# Revit family: Sanitary_Toilet-Cisterns_Sanindusa_Easy-3-6L-Flushing-Plate
name_source: partatom
category: Plumbing Fixtures
revit_build: Autodesk Revit 2018 (Build: 20170223_1515(x64)
units: mm (PartAtom-declared; Revit-internal decimal feet)

## family parameters
Always vertical = Yes
Cut with Voids When Loaded = No
OmniClass Number = 23.45.00.00
OmniClass Title = Sanitary, Laundry, and Cleaning Equipment
Part Type = Normal
Room Calculation Point = No
Round Connector Dimension = Use Diameter
Shared = No
Work Plane-Based = No

## types (1)
- PlacaDescargaEasyEstruturaSanfix4002311
    AssetType = Fixed
    Color = Silver
    Constituents = All parts necessary to install flushing plate are included.
150 mm PVC flexible hose; ABS shower bracket, with adjustable height; Fixing Kit.
    Cost = 0 $
    Description = Flushing plate for mechanism 3/6Lts
    Edition number = 1
    Element Type = FLUSH PLATES
    Features = Plate for dual flush with frontal activation.
    Finish = Chrome plated
    FlushType = DualFlush
    Installation Instructions = https://www.tec.sanindusa.pt
    InstallationDate = 1900-12-31T23:59:59
    Manufacturer = Sanindusa
    ManufacturerName = Sanindusa
    ManufacturerURL = www.tec.sanindusa.pt
    Material = ABS
    ModelNumber = 4002311
    ModelReference = Easy
    Name = Easy 3|6L flushing plate
    NominalHeight = 170 mm  [stored 0.557743 ft]
    NominalLength = 255 mm  [stored 0.836614 ft]
    NominalWidth = 18 mm  [stored 0.0590551 ft]
    Pre-defined type (IFC) = FURNISHING ELEMENT
    Product Guid = 9c633c56-7eef-49a4-ae7a-a13ab5ee2c1d
    Product data url = https://bimobject.com
    ProductInformation = https://www.tec.sanindusa.pt
    ProductionYear = 2017
    Shape = rectangular
    Size = 26x2x17
    Type (IFC) = IfcFurnitureType
    URL = www.tec.sanindusa.pt
    Uniclass2015Code = Pr_40_20_93_87
    Uniclass2015Title = WC cistern fittings
    Uniclass2015Version = Products v1.6
    Version = 2
    WarrantyDescription = https://www.tec.sanindusa.pt
    WarrantyDurationParts = 2
    WarrantyDurationUnit = year
    WarrantyStartDate = 1900-12-31T23:59:59
1900-12-31T23:59:59
    Weight = 0.80 kg

note: [stored X ft] marks values corroborated as IEEE doubles in the binary element streams (Revit-internal decimal feet)

## geometry (parser evidence)
native form markers: Sweep x8
no freeform markers — native parametric forms only
